# Revit family: Sanitary_Other-Sanitary_AXOR_48798CHN-AXOR-One-Basic-set-for-showerpi_
name_source: partatom
category: Plumbing Fixtures
revit_build: Autodesk Revit 2018 (Build: 20170223_1515(x64)
units: mm (PartAtom-declared; Revit-internal decimal feet)

## family parameters
Always vertical = No
Cut with Voids When Loaded = No
OmniClass Number = 23.40.20.00
OmniClass Title = General Furniture and Specialties
Part Type = Normal
Room Calculation Point = No
Round Connector Dimension = Use Diameter
Shared = No
Work Plane-Based = No

## types (1)
- n.a.
    Always visible = Yes
    BIMobject category = Other Sanitary
    Design country = Germany
    EAN code = 4059625329351
    Edition number = 1
    IFC Classification = Sanitary Terminal
    Installation instructions = https://www.axor-design.com
    Manufacturer country = Germany
    Manufacturer name = AXOR
    Material 1 = AXOR - AXOR One - Brass
    Material 2 = AXOR - AXOR One - Green
    Material 3 = AXOR - AXOR One - Stainless Steel
    Material 4 = AXOR - AXOR One - Black
    Material main = Chrome
    Product Guid = db50aea0-4122-4643-b5cb-13d05a597709
    Product SKU = 48798CHN
    Product data url = https://www.bimobject.com
    Product family = AXOR One
    Product group = Concealed Basic set bath/shower mixers
    Product name = 48798CHN AXOR One Basic set for showerpipe
    Product url = https://www.axor-design.com
    QR code = https://www.bimobject.com
    Technical description = https://www.axor-design.com

## geometry (parser evidence)
native form markers: Sweep x3
no freeform markers — native parametric forms only
